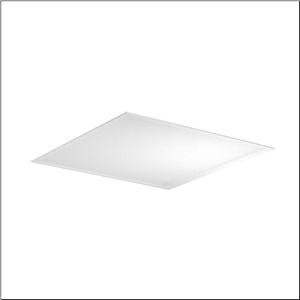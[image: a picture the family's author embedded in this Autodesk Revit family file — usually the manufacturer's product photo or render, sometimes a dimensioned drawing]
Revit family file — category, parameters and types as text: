
# Revit family: apollon_r__21_square_51mq12w72m14_a180
name_source: partatom
category: Lighting Fixtures
units: mm (PartAtom-declared; Revit-internal decimal feet)

## family parameters
Cut with Voids When Loaded = No
Host = Face
Light Source = No
Part Type = Normal
Room Calculation Point = No
Round Connector Dimension = Use Diameter
Shared = No

## types (1)
- --- (1 x LED, 4200 lm, 24.2 W, 4000K)
    Apparent Load = 24 VA
    CIE Flux Codes = 60 87 97 100 100
    Color Rendering = 80
    Color Temperature = 4000K
    Default Elevation = 1800 mm
    Description = Apollon® 21 square, office luminaire, primary optical cover: micro prismatic cover, of PMMA, CAT 2 (L<= 3000cd/m²), light emission: direct distribution, primary light characteristic: symmetric, installation type: lay-in mounting, LED, rated luminous flux: 4.200lm, luminous efficacy: 174lm/W, light colour: 830/840, colour temperature: 3000/4000K, with terminal, 3-pole, mains connection: 220..240V, AC/DC, 0/50..60Hz, rated input power: 24.2W, housing, of aluminium, coated, traffic white (RAL 9016), module: M600, length: 595mm, width: 595mm, height: 30mm, housing upper side, of sheet steel, galvanised, protection rating (complete): IP20, protection rating (lamp compartment, on room side): IP50, insulation class (complete): insulation class II (safety insulation), certification: CE, ENEC, impact resistance: IK03, permissible operating ambient temperature: -20..+45°C, permissible storage temperature: -40..+80°C, packaging unit: 1 piece
    Height = 0 mm  [stored 0 ft]
    Lamp = 1 x LED
    Lamp Light Flux = 4200 lm
    Lamp Power = 24.2 W
    Lamp count = 1
    Length = 595 mm
    Luminous efficacy = 174 lm/W
    Manufacturer = Siteco
    ModVariant = No
    Model = 51MQ12W72M14
    Mounting Place = Ceiling
    Mounting Type = Recessed
    Number of Poles = 1
    OnlyDefault = Yes
    Power Factor = 1
    Product Name = Apollon® 21 square
    Product group = office luminaire | ceiling recessed
    ProductGroupID = 401
    Protection Class = Protection class II
    Protection Degree = IP 20
    RLX_Detail_Level = 1
    RLX_Emergency_Light_Flux = 0 lm
    RLX_Emergency_Type = 0
    RLX_Emergency_Type_DB = No
    RlxData = <blob elided: 12709 chars, md5=892d6c68>
    Socket = socket
    Standby Power = 0 W
    System Light Flux = 4200 lm
    System Power = 24 W
    Type Comments = factory setting
    Type Image = l_1291049.jpg
    URL = http://relux.com
    VarID = @adj_008845
    Voltage = 0 V
    Weight = 0.00 kg
    Width = 595 mm

note: [stored X ft] marks values corroborated as IEEE doubles in the binary element streams (Revit-internal decimal feet)

## geometry (parser evidence)
native form markers: Sweep x10
no freeform markers — native parametric forms only
